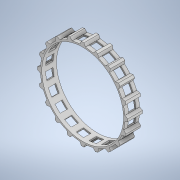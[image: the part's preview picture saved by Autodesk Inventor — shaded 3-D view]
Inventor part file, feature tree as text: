
AUTODESK INVENTOR PART (.ipt)
format: ipt  version: 2020 (Build 240168000, 168)  size: 419,328 bytes
history: native  units: mm
features: extrude x4, sketch x3, other x2, chamfer x2, pattern_circular x1
ambient origin geometry x8: Origin, YZ Plane, XZ Plane, XY Plane, X Axis, Y Axis, Z Axis, Center Point
bodies: Body1 (feature_tree)
feature tree (12):
  other  "Bryła1"
  extrude  "Wyciągnięcie proste1"  Depth=111.109mm
  other  "Płaszczyzna konstrukcyjna1"
  extrude  "Wyciągnięcie proste2"  Depth=2.0mm
  chamfer  "Faza1"  Distance=20.0mm
  chamfer  "Faza2"  Distance=7.528mm
  pattern_circular  "Szyk kołowy1"  [2 undecoded]
  sketch  "Szkic3"
  extrude  "Wyciągnięcie proste3"  Depth=2.0mm TaperAngle=45.0deg
  extrude  "Wyciągnięcie proste4"  Depth=2.0mm TaperAngle=45.0deg
  sketch  "Szkic1"
  sketch  "Szkic2"
note: 2 required parameter values undecoded (feature->parameter linkage not recoverable at this tier; creation-order binding heuristic only, values carry confidence <= 0.55)
